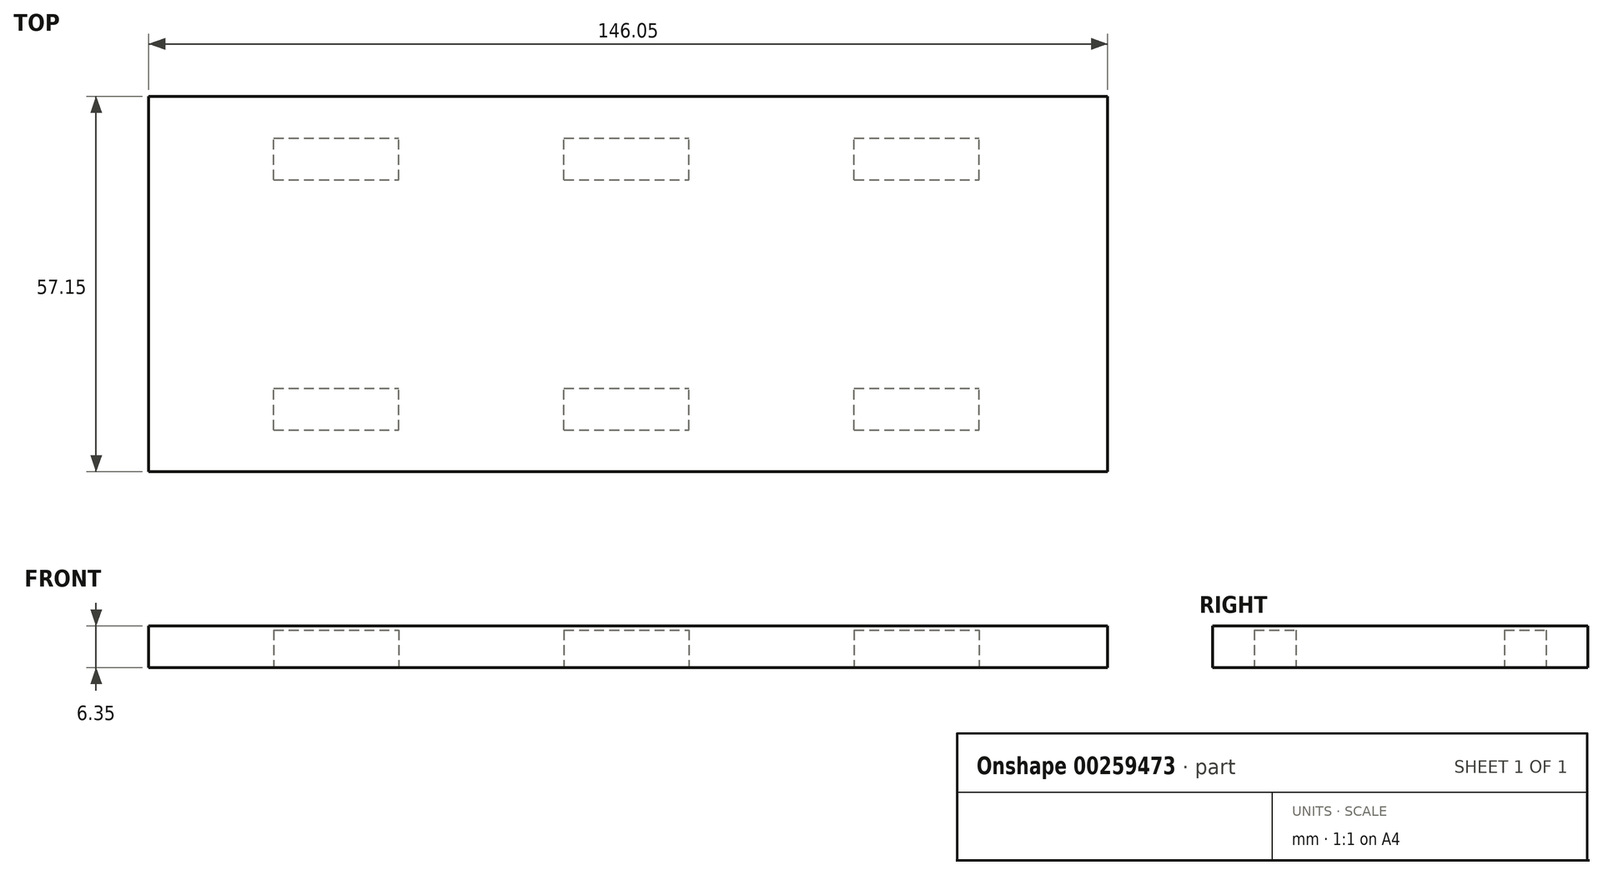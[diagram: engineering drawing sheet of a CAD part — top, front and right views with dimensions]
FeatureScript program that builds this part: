
annotation { "Feature Type Name" : "Feature", "Feature Type Description" : "" }
export const myFeature = defineFeature(function(context is Context, id is Id, definition is map)
    precondition{}
    {
        {
            var Q0;
            Q0=qCreatedBy(makeId("Top.planeOp"),FACE);
            var sketch = newSketch(context, id + "F0", { "sketchPlane" : qUnion([Q0])});
            skLineSegment(sketch, "E0.bottom", {"start": v(0, 0) * mm, "end": v(146.05, 0) * mm});
            skLineSegment(sketch, "E0.top", {"start": v(0, -57.15) * mm, "end": v(146.05, -57.15) * mm});
            skLineSegment(sketch, "E0.left", {"start": v(0, 0) * mm, "end": v(0, -57.15) * mm});
            skLineSegment(sketch, "E0.right", {"start": v(146.05, 0) * mm, "end": v(146.05, -57.15) * mm});
            skSolve(sketch);
        }
        {
            var Q0;
            Q0=makeQuery(id+"F0.imprint","IMPRINT",FACE,{"disambiguationData":[TD([[makeQuery(id+"F0.imprint","IMPRINT",EDGE,{"derivedFrom":sQuery(id+"F0.wireOp",EDGE,"E0.bottom")}),-1.0]])]});
            extrude(context, id + "F1", {"entities" : qUnion([Q0]), "depth" : 6.35 * mm});
        }
        {
            var Q0;
            Q0=makeQuery(id+"F1.opExtrude","CAP_FACE",FACE,{"disambiguationData":[OSD([sQuery(id+"F0.wireOp",EDGE,"E0.bottom"),sQuery(id+"F0.wireOp",EDGE,"E0.top"),sQuery(id+"F0.wireOp",EDGE,"E0.left"),sQuery(id+"F0.wireOp",EDGE,"E0.right")])],"isStart":true});
            var sketch = newSketch(context, id + "F2", { "sketchPlane" : qUnion([Q0])});
            skLineSegment(sketch, "E1.bottom", {"start": v(19.05, 50.8) * mm, "end": v(38.1, 50.8) * mm});
            skLineSegment(sketch, "E1.top", {"start": v(19.05, 44.45) * mm, "end": v(38.1, 44.45) * mm});
            skLineSegment(sketch, "E1.left", {"start": v(19.05, 50.8) * mm, "end": v(19.05, 44.45) * mm});
            skLineSegment(sketch, "E1.right", {"start": v(38.1, 50.8) * mm, "end": v(38.1, 44.45) * mm});
            skLineSegment(sketch, "E2.0.1.0", {"start": v(38.1, 12.7) * mm, "end": v(38.1, 6.35) * mm});
            skLineSegment(sketch, "E2.0.1.1", {"start": v(19.05, 12.7) * mm, "end": v(38.1, 12.7) * mm});
            skLineSegment(sketch, "E2.0.1.2", {"start": v(19.05, 12.7) * mm, "end": v(19.05, 6.35) * mm});
            skLineSegment(sketch, "E2.0.1.3", {"start": v(19.05, 6.35) * mm, "end": v(38.1, 6.35) * mm});
            skLineSegment(sketch, "E2.1.0.0", {"start": v(82.3, 50.8) * mm, "end": v(82.3, 44.45) * mm});
            skLineSegment(sketch, "E2.1.0.1", {"start": v(63.25, 50.8) * mm, "end": v(82.3, 50.8) * mm});
            skLineSegment(sketch, "E2.1.0.2", {"start": v(63.25, 50.8) * mm, "end": v(63.25, 44.45) * mm});
            skLineSegment(sketch, "E2.1.0.3", {"start": v(63.25, 44.45) * mm, "end": v(82.3, 44.45) * mm});
            skLineSegment(sketch, "E2.1.1.0", {"start": v(82.3, 12.7) * mm, "end": v(82.3, 6.35) * mm});
            skLineSegment(sketch, "E2.1.1.1", {"start": v(63.25, 12.7) * mm, "end": v(82.3, 12.7) * mm});
            skLineSegment(sketch, "E2.1.1.2", {"start": v(63.25, 12.7) * mm, "end": v(63.25, 6.35) * mm});
            skLineSegment(sketch, "E2.1.1.3", {"start": v(63.25, 6.35) * mm, "end": v(82.3, 6.35) * mm});
            skLineSegment(sketch, "E2.2.0.0", {"start": v(126.5, 50.8) * mm, "end": v(126.5, 44.45) * mm});
            skLineSegment(sketch, "E2.2.0.1", {"start": v(107.44, 50.8) * mm, "end": v(126.5, 50.8) * mm});
            skLineSegment(sketch, "E2.2.0.2", {"start": v(107.44, 50.8) * mm, "end": v(107.44, 44.45) * mm});
            skLineSegment(sketch, "E2.2.0.3", {"start": v(107.44, 44.45) * mm, "end": v(126.5, 44.45) * mm});
            skLineSegment(sketch, "E2.2.1.0", {"start": v(126.5, 12.7) * mm, "end": v(126.5, 6.35) * mm});
            skLineSegment(sketch, "E2.2.1.1", {"start": v(107.44, 12.7) * mm, "end": v(126.5, 12.7) * mm});
            skLineSegment(sketch, "E2.2.1.2", {"start": v(107.44, 12.7) * mm, "end": v(107.44, 6.35) * mm});
            skLineSegment(sketch, "E2.2.1.3", {"start": v(107.44, 6.35) * mm, "end": v(126.5, 6.35) * mm});
            skLineSegment(sketch, "E2.direction1", {"start": v(38.1, 44.45) * mm, "end": v(82.3, 44.45) * mm, "construction": true});
            skLineSegment(sketch, "E2.direction2", {"start": v(38.1, 44.45) * mm, "end": v(38.1, 6.35) * mm, "construction": true});
            skSolve(sketch);
        }
        {
            var Q0;
            Q0=makeQuery(id+"F2.imprint","IMPRINT",FACE,{"disambiguationData":[TD([[makeQuery(id+"F2.imprint","IMPRINT",EDGE,{"derivedFrom":sQuery(id+"F2.wireOp",EDGE,"E1.bottom")}),-1.0]])]});
            var Q1;
            Q1=makeQuery(id+"F2.imprint","IMPRINT",FACE,{"disambiguationData":[TD([[makeQuery(id+"F2.imprint","IMPRINT",EDGE,{"derivedFrom":sQuery(id+"F2.wireOp",EDGE,"E2.1.0.0")}),-1.0]])]});
            var Q2;
            Q2=makeQuery(id+"F2.imprint","IMPRINT",FACE,{"disambiguationData":[TD([[makeQuery(id+"F2.imprint","IMPRINT",EDGE,{"derivedFrom":sQuery(id+"F2.wireOp",EDGE,"E2.2.0.0")}),-1.0]])]});
            var Q3;
            Q3=makeQuery(id+"F2.imprint","IMPRINT",FACE,{"disambiguationData":[TD([[makeQuery(id+"F2.imprint","IMPRINT",EDGE,{"derivedFrom":sQuery(id+"F2.wireOp",EDGE,"E2.0.1.0")}),-1.0]])]});
            var Q4;
            Q4=makeQuery(id+"F2.imprint","IMPRINT",FACE,{"disambiguationData":[TD([[makeQuery(id+"F2.imprint","IMPRINT",EDGE,{"derivedFrom":sQuery(id+"F2.wireOp",EDGE,"E2.1.1.0")}),-1.0]])]});
            var Q5;
            Q5=makeQuery(id+"F2.imprint","IMPRINT",FACE,{"disambiguationData":[TD([[makeQuery(id+"F2.imprint","IMPRINT",EDGE,{"derivedFrom":sQuery(id+"F2.wireOp",EDGE,"E2.2.1.0")}),-1.0]])]});
            extrude(context, id + "F3", {"entities" : qUnion([Q0, Q1, Q2, Q3, Q4, Q5]), "operationType" : NewBodyOperationType.REMOVE, "oppositeDirection" : true, "depth" : 5.7 * mm});
        }
    });
